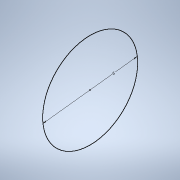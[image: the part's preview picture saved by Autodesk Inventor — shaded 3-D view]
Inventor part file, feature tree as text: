
AUTODESK INVENTOR PART (.ipt)
format: ipt  version: 2021.1 (Build 251245010, 245A)  size: 84,992 bytes
history: native  units: mm
features: sketch x1
ambient origin geometry x8: Origin, YZ Plane, XZ Plane, XY Plane, X Axis, Y Axis, Z Axis, Center Point
feature tree (1):
  sketch  "Sketch1"  dims[d0=6.0mm]
